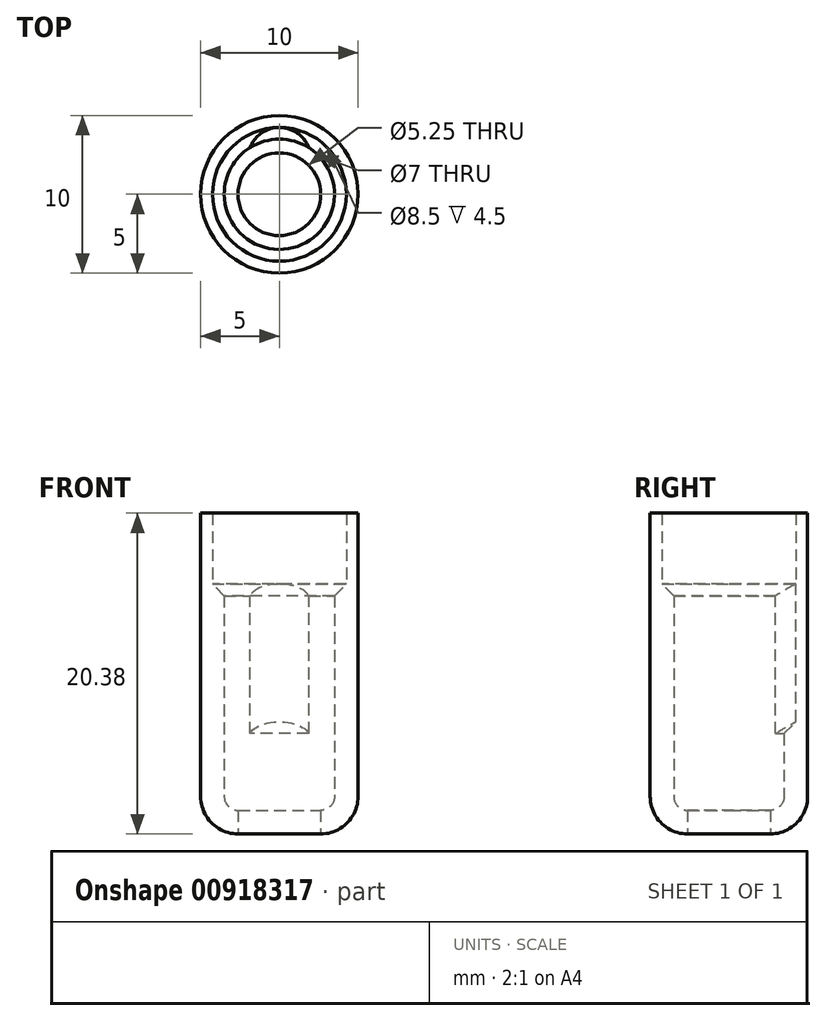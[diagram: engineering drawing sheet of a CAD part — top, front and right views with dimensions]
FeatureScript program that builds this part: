
annotation { "Feature Type Name" : "Feature", "Feature Type Description" : "" }
export const myFeature = defineFeature(function(context is Context, id is Id, definition is map)
    precondition{}
    {
        {
            var Q0;
            Q0=qCreatedBy(makeId("Front.planeOp"),FACE);
            var sketch = newSketch(context, id + "F0", { "sketchPlane" : qUnion([Q0])});
            skLineSegment(sketch, "E0", {"start": v(0, 0) * mm, "end": v(0, 20.37) * mm, "construction": true});
            skLineSegment(sketch, "E1", {"start": v(-5, 20.38) * mm, "end": v(-5, 2.38) * mm});
            skArc(sketch, "E2", {"start": v(-5, 2.38) * mm, "mid": v(-4.3, 0.7) * mm, "end": v(-2.62, 0) * mm});
            skLineSegment(sketch, "E3", {"start": v(-5, 20.37) * mm, "end": v(0, 20.37) * mm, "construction": true});
            skLineSegment(sketch, "E4", {"start": v(-2.62, 0) * mm, "end": v(0, 0) * mm, "construction": true});
            skLineSegment(sketch, "E5", {"start": v(-5, 20.37) * mm, "end": v(-4.25, 20.37) * mm});
            skLineSegment(sketch, "E6", {"start": v(-4.25, 20.37) * mm, "end": v(-4.25, 15.87) * mm});
            skLineSegment(sketch, "E7", {"start": v(-4.25, 15.87) * mm, "end": v(-3.5, 15.87) * mm, "construction": true});
            skLineSegment(sketch, "E8", {"start": v(-3.5, 15.12) * mm, "end": v(-3.5, 2.37) * mm});
            skArc(sketch, "E9", {"start": v(-3.5, 2.37) * mm, "mid": v(-3.24, 1.76) * mm, "end": v(-2.62, 1.5) * mm});
            skLineSegment(sketch, "E10", {"start": v(-2.62, 1.5) * mm, "end": v(-2.62, 0) * mm});
            skLineSegment(sketch, "E11", {"start": v(-4.25, 15.87) * mm, "end": v(-3.5, 15.12) * mm});
            skSolve(sketch);
        }
        {
            var Q0;
            Q0 = qSketchRegion(id + "F0", true);
            var Q1;
            Q1=sQuery(id+"F0.wireOp",EDGE,"E0");
            revolve(context, id + "F1", {"surfaceOperationType" : NewSurfaceOperationType.NEW, "entities" : qUnion([Q0]), "axis" : qUnion([Q1]), "revolveType" : RevolveType.FULL});
        }
        {
            var Q0;
            Q0=makeQuery(id+"F1.opRevolve","SWEPT_FACE",FACE,{"disambiguationData":[OSD([sQuery(id+"F0.wireOp",EDGE,"E5")])]});
            var sketch = newSketch(context, id + "F2", { "sketchPlane" : qUnion([Q0])});
            skCircle(sketch, "E12", {"center": v(0, 2.25) * mm, "radius": 2 * mm});
            skSolve(sketch);
        }
        {
            var Q0;
            Q0 = qSketchRegion(id + "F2", true);
            extrude(context, id + "F3", {"entities" : qUnion([Q0]), "operationType" : NewBodyOperationType.REMOVE, "oppositeDirection" : true, "depth" : 13 * mm, "offsetDistance" : 25 * mm});
        }
        {
            var Q0;
            Q0=makeQuery(id+"F3.boolean.opBoolean","INTERSECT",EDGE,{"derivedFrom":[makeQuery(id+"F1.opRevolve","SWEPT_FACE",FACE,{"disambiguationData":[OSD([sQuery(id+"F0.wireOp",EDGE,"E8")])]}),makeQuery(id+"F3.opExtrude","CAP_FACE",FACE,{"disambiguationData":[OSD([sQuery(id+"F2.wireOp",EDGE,"E12")])],"isStart":false})]});
            chamfer(context, id + "F4", {"entities" : qUnion([Q0]), "chamferType" : ChamferType.OFFSET_ANGLE, "width" : 1 * mm, "oppositeDirection" : false, "angle" : 45 * degree, "tangentPropagation" : true});
        }
    });
